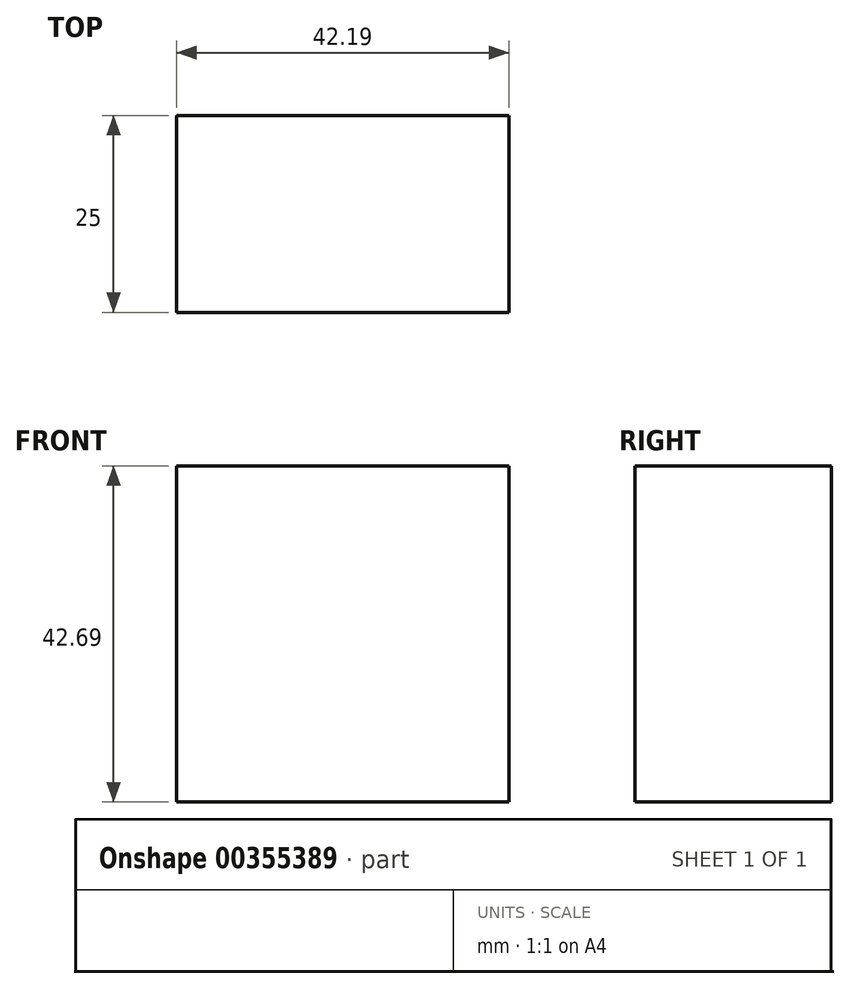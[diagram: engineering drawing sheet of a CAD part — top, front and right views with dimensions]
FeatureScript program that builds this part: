
annotation { "Feature Type Name" : "Feature", "Feature Type Description" : "" }
export const myFeature = defineFeature(function(context is Context, id is Id, definition is map)
    precondition{}
    {
        {
            var Q0;
            Q0=qCreatedBy(makeId("Front.planeOp"),FACE);
            var sketch = newSketch(context, id + "F0", { "sketchPlane" : qUnion([Q0])});
            skLineSegment(sketch, "E0.bottom", {"start": v(-48.68, -5.3) * mm, "end": v(-6.5, -5.3) * mm});
            skLineSegment(sketch, "E0.top", {"start": v(-48.68, 37.4) * mm, "end": v(-6.5, 37.4) * mm});
            skLineSegment(sketch, "E0.left", {"start": v(-48.68, -5.3) * mm, "end": v(-48.68, 37.4) * mm});
            skLineSegment(sketch, "E0.right", {"start": v(-6.5, -5.3) * mm, "end": v(-6.5, 37.4) * mm});
            skPoint(sketch, "E0.middle", {"position": v(-27.59, 16.05) * mm});
            skSolve(sketch);
        }
        {
            var Q0;
            Q0=makeQuery(id+"F0.imprint","IMPRINT",FACE,{"disambiguationData":[TD([[makeQuery(id+"F0.imprint","IMPRINT",EDGE,{"derivedFrom":sQuery(id+"F0.wireOp",EDGE,"E0.bottom")}),1.0]])]});
            extrude(context, id + "F1", {"entities" : qUnion([Q0]), "depth" : 25 * mm});
        }
    });
